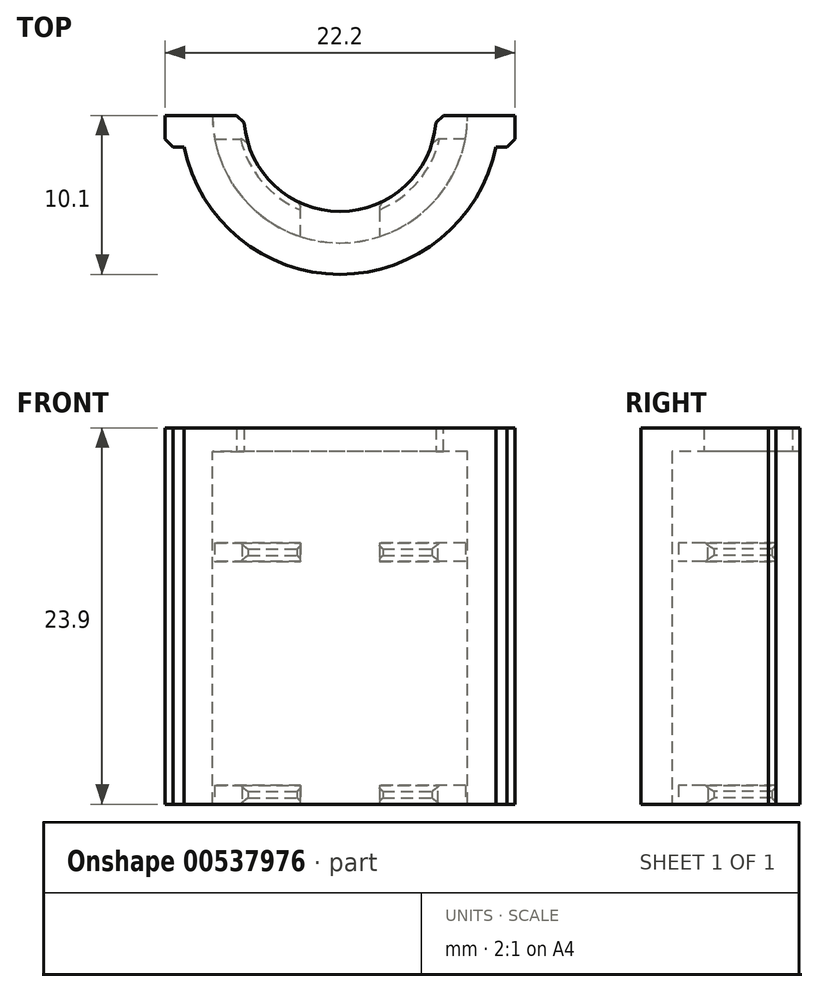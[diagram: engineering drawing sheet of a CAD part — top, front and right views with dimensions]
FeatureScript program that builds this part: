
annotation { "Feature Type Name" : "Feature", "Feature Type Description" : "" }
export const myFeature = defineFeature(function(context is Context, id is Id, definition is map)
    precondition{}
    {
        {
            var Q0;
            Q0=qCreatedBy(makeId("Front.planeOp"),FACE);
            var sketch = newSketch(context, id + "F0", { "sketchPlane" : qUnion([Q0])});
            skLineSegment(sketch, "E0.bottom", {"start": v(-8.1, 0) * mm, "end": v(-10.1, 0) * mm});
            skLineSegment(sketch, "E0.top", {"start": v(-8.1, 29) * mm, "end": v(-10.1, 29) * mm});
            skLineSegment(sketch, "E0.left", {"start": v(-8.1, 0) * mm, "end": v(-8.1, 29) * mm});
            skLineSegment(sketch, "E0.right", {"start": v(-10.1, 0) * mm, "end": v(-10.1, 29) * mm});
            skLineSegment(sketch, "E1.bottom", {"start": v(-8.1, 23.2) * mm, "end": v(-6.1, 23.2) * mm});
            skLineSegment(sketch, "E1.top", {"start": v(-8.1, 22) * mm, "end": v(-6.1, 22) * mm});
            skLineSegment(sketch, "E1.left", {"start": v(-8.1, 23.2) * mm, "end": v(-8.1, 22) * mm});
            skLineSegment(sketch, "E1.right", {"start": v(-6.1, 23.2) * mm, "end": v(-6.1, 22) * mm});
            skLineSegment(sketch, "E2", {"start": v(0, 0) * mm, "end": v(0, 37.94) * mm, "construction": true});
            skLineSegment(sketch, "E3.bottom", {"start": v(-8.1, 17) * mm, "end": v(-6.1, 17) * mm});
            skLineSegment(sketch, "E3.top", {"start": v(-8.1, 15.8) * mm, "end": v(-6.1, 15.8) * mm});
            skLineSegment(sketch, "E3.left", {"start": v(-8.1, 17) * mm, "end": v(-8.1, 15.8) * mm});
            skLineSegment(sketch, "E3.right", {"start": v(-6.1, 17) * mm, "end": v(-6.1, 15.8) * mm});
            skLineSegment(sketch, "E4.bottom", {"start": v(-8.1, 7.8) * mm, "end": v(-6.1, 7.8) * mm});
            skLineSegment(sketch, "E4.top", {"start": v(-8.1, 6.6) * mm, "end": v(-6.1, 6.6) * mm});
            skLineSegment(sketch, "E4.left", {"start": v(-8.1, 7.8) * mm, "end": v(-8.1, 6.6) * mm});
            skLineSegment(sketch, "E4.right", {"start": v(-6.1, 7.8) * mm, "end": v(-6.1, 6.6) * mm});
            skLineSegment(sketch, "E5.bottom", {"start": v(-8.1, 13.9) * mm, "end": v(-6.1, 13.9) * mm});
            skLineSegment(sketch, "E5.top", {"start": v(-8.1, 12.7) * mm, "end": v(-6.1, 12.7) * mm});
            skLineSegment(sketch, "E5.left", {"start": v(-8.1, 13.9) * mm, "end": v(-8.1, 12.7) * mm});
            skLineSegment(sketch, "E5.right", {"start": v(-6.1, 13.9) * mm, "end": v(-6.1, 12.7) * mm});
            skLineSegment(sketch, "E6.bottom", {"start": v(-10.1, 29) * mm, "end": v(-6.1, 29) * mm});
            skLineSegment(sketch, "E6.top", {"start": v(-10.1, 30.5) * mm, "end": v(-6.1, 30.5) * mm});
            skLineSegment(sketch, "E6.left", {"start": v(-10.1, 29) * mm, "end": v(-10.1, 30.5) * mm});
            skLineSegment(sketch, "E6.right", {"start": v(-6.1, 29) * mm, "end": v(-6.1, 30.5) * mm});
            skSolve(sketch);
        }
        {
            var Q0;
            {var subQ3=sQuery(id+"F0.wireOp",EDGE,"E0.bottom");Q0=makeQuery(id+"F0.imprint","IMPRINT",FACE,{"disambiguationData":[TD([[makeQuery(id+"F0.imprint","IMPRINT",EDGE,{"derivedFrom":subQ3}),-1.0]])]});}
            var Q1;
            Q1=makeQuery(id+"F0.imprint","IMPRINT",FACE,{"disambiguationData":[TD([[makeQuery(id+"F0.imprint","IMPRINT",EDGE,{"derivedFrom":sQuery(id+"F0.wireOp",EDGE,"E1.bottom")}),-1.0]])]});
            var Q2;
            Q2=makeQuery(id+"F0.imprint","IMPRINT",FACE,{"disambiguationData":[TD([[makeQuery(id+"F0.imprint","IMPRINT",EDGE,{"derivedFrom":sQuery(id+"F0.wireOp",EDGE,"E4.bottom")}),-1.0]])]});
            var Q3;
            Q3=makeQuery(id+"F0.imprint","IMPRINT",FACE,{"disambiguationData":[TD([[makeQuery(id+"F0.imprint","IMPRINT",EDGE,{"derivedFrom":sQuery(id+"F0.wireOp",EDGE,"P9eNyCsC-jT8K-Uow4-PnuW-2JQdisNrIWnP.bottom")}),-1.0]])]});
            var Q4;
            Q4=makeQuery(id+"F0.imprint","IMPRINT",FACE,{"disambiguationData":[TD([[makeQuery(id+"F0.imprint","IMPRINT",EDGE,{"derivedFrom":sQuery(id+"F0.wireOp",EDGE,"MsjulPPt-OwuK-sYkB-IQlA-wEg1vznDjQIO.bottom")}),-1.0]])]});
            var Q5;
            Q5=makeQuery(id+"F0.imprint","IMPRINT",FACE,{"disambiguationData":[TD([[makeQuery(id+"F0.imprint","IMPRINT",EDGE,{"derivedFrom":sQuery(id+"F0.wireOp",EDGE,"1A2XH9Hr-huH4-Xs39-ezpS-GpKjiSIjocRw.bottom")}),1.0]])]});
            var Q6;
            Q6=makeQuery(id+"F0.imprint","IMPRINT",FACE,{"disambiguationData":[TD([[makeQuery(id+"F0.imprint","IMPRINT",EDGE,{"derivedFrom":sQuery(id+"F0.wireOp",EDGE,"E6.top")}),-1.0]])]});
            var Q7;
            Q7=sQuery(id+"F0.wireOp",EDGE,"E2");
            revolve(context, id + "F1", {"entities" : qUnion([Q0, Q1, Q2, Q3, Q4, Q5, Q6]), "axis" : qUnion([Q7]), "revolveType" : RevolveType.ONE_DIRECTION, "angle" : 180 * degree});
        }
        {
            var Q0;
            Q0=makeQuery(id+"F1.opRevolve","SWEPT_FACE",FACE,{"disambiguationData":[OSD([sQuery(id+"F0.wireOp",EDGE,"E0.bottom")])]});
            var sketch = newSketch(context, id + "F2", { "sketchPlane" : qUnion([Q0])});
            skArc(sketch, "E7", {"start": v(2.5, 7.7) * mm, "mid": v(0, 8.1) * mm, "end": v(-2.5, 7.7) * mm});
            skLineSegment(sketch, "E8", {"start": v(2.5, 7.7) * mm, "end": v(2.5, 5.56) * mm});
            skLineSegment(sketch, "E9", {"start": v(2.5, 5.56) * mm, "end": v(-2.5, 5.56) * mm});
            skLineSegment(sketch, "E10", {"start": v(-2.5, 5.56) * mm, "end": v(-2.5, 7.7) * mm});
            skLineSegment(sketch, "E11", {"start": v(-5.91, 1.5) * mm, "end": v(-7.96, 1.5) * mm});
            skLineSegment(sketch, "E12", {"start": v(-5.91, 1.5) * mm, "end": v(-5.91, 0) * mm});
            skLineSegment(sketch, "E13", {"start": v(-5.91, 0) * mm, "end": v(-8.1, 0) * mm});
            skArc(sketch, "E14", {"start": v(-7.96, 1.5) * mm, "mid": v(-8.06, 0.75) * mm, "end": v(-8.1, 0) * mm});
            skLineSegment(sketch, "E15.MirrorCS", {"start": v(5.91, 1.5) * mm, "end": v(5.91, 0) * mm});
            skLineSegment(sketch, "E16.MirrorCS", {"start": v(5.91, 1.5) * mm, "end": v(7.96, 1.5) * mm});
            skLineSegment(sketch, "E17.MirrorCS", {"start": v(5.91, 0) * mm, "end": v(8.1, 0) * mm});
            skArc(sketch, "E18.MirrorCS", {"start": v(7.96, 1.5) * mm, "mid": v(8.06, 0.75) * mm, "end": v(8.1, 0) * mm});
            skSolve(sketch);
        }
        {
            var Q0;
            Q0=makeQuery(id+"F2.imprint","IMPRINT",FACE,{"disambiguationData":[TD([[makeQuery(id+"F2.imprint","IMPRINT",EDGE,{"derivedFrom":sQuery(id+"F2.wireOp",EDGE,"E7")}),1.0]])]});
            var Q1;
            Q1=makeQuery(id+"F2.imprint","IMPRINT",FACE,{"disambiguationData":[TD([[makeQuery(id+"F2.imprint","IMPRINT",EDGE,{"derivedFrom":sQuery(id+"F2.wireOp",EDGE,"E15.MirrorCS")}),1.0]])]});
            var Q2;
            Q2=makeQuery(id+"F2.imprint","IMPRINT",FACE,{"disambiguationData":[TD([[makeQuery(id+"F2.imprint","IMPRINT",EDGE,{"derivedFrom":sQuery(id+"F2.wireOp",EDGE,"E11")}),1.0]])]});
            var Q3;
            Q3=makeQuery(id+"F1.opRevolve","SWEPT_FACE",FACE,{"disambiguationData":[OSD([sQuery(id+"F0.wireOp",EDGE,"E6.bottom")])]});
            extrude(context, id + "F3", {"entities" : qUnion([Q0, Q1, Q2]), "operationType" : NewBodyOperationType.REMOVE, "endBound" : BoundingType.UP_TO_SURFACE, "oppositeDirection" : true, "depth" : 25 * mm, "endBoundEntityFace" : qUnion([Q3]), "offsetDistance" : 25 * mm});
        }
        {
            var Q0;
            Q0=makeQuery(id+"F1.opRevolve","SWEPT_FACE",FACE,{"disambiguationData":[OSD([sQuery(id+"F0.wireOp",EDGE,"E0.bottom")])]});
            var sketch = newSketch(context, id + "F4", { "sketchPlane" : qUnion([Q0])});
            skLineSegment(sketch, "E19.bottom", {"start": v(-9.1, 0) * mm, "end": v(-11.1, 0) * mm});
            skLineSegment(sketch, "E19.top", {"start": v(-9.1, 2) * mm, "end": v(-11.1, 2) * mm});
            skLineSegment(sketch, "E19.left", {"start": v(-9.1, 0) * mm, "end": v(-9.1, 2) * mm});
            skLineSegment(sketch, "E19.right", {"start": v(-11.1, 0) * mm, "end": v(-11.1, 2) * mm});
            skLineSegment(sketch, "E20.MirrorCS", {"start": v(9.1, 2) * mm, "end": v(11.1, 2) * mm});
            skLineSegment(sketch, "E21.MirrorCS", {"start": v(9.1, 0) * mm, "end": v(9.1, 2) * mm});
            skLineSegment(sketch, "E22.MirrorCS", {"start": v(9.1, 0) * mm, "end": v(11.1, 0) * mm});
            skLineSegment(sketch, "E23.MirrorCS", {"start": v(11.1, 0) * mm, "end": v(11.1, 2) * mm});
            skSolve(sketch);
        }
        {
            var Q0;
            {var subQ0=sQuery(id+"F4.wireOp",EDGE,"E23.MirrorCS");Q0=makeQuery(id+"F4.imprint","IMPRINT",FACE,{"disambiguationData":[TD([[makeQuery(id+"F4.imprint","IMPRINT",EDGE,{"derivedFrom":subQ0}),1.0]])]});}
            var Q1;
            {var subQ3=sQuery(id+"F4.wireOp",EDGE,"E19.right");Q1=makeQuery(id+"F4.imprint","IMPRINT",FACE,{"disambiguationData":[TD([[makeQuery(id+"F4.imprint","IMPRINT",EDGE,{"derivedFrom":subQ3}),-1.0]])]});}
            var Q2;
            Q2=makeQuery(id+"F1.opRevolve","SWEPT_FACE",FACE,{"disambiguationData":[OSD([sQuery(id+"F0.wireOp",EDGE,"E6.top")])]});
            extrude(context, id + "F5", {"entities" : qUnion([Q0, Q1]), "operationType" : NewBodyOperationType.ADD, "endBound" : BoundingType.UP_TO_SURFACE, "oppositeDirection" : true, "depth" : 25 * mm, "endBoundEntityFace" : qUnion([Q2]), "offsetDistance" : 25 * mm});
        }
        {
            var Q0;
            {var subQ7=sQuery(id+"F4.wireOp",EDGE,"E19.left");Q0=makeQuery(id+"F4.imprint","IMPRINT",FACE,{"disambiguationData":[TD([[makeQuery(id+"F4.imprint","IMPRINT",EDGE,{"derivedFrom":subQ7}),-1.0]])]});}
            var Q1;
            {var subQ3=sQuery(id+"F4.wireOp",EDGE,"E19.right");Q1=makeQuery(id+"F4.imprint","IMPRINT",FACE,{"disambiguationData":[TD([[makeQuery(id+"F4.imprint","IMPRINT",EDGE,{"derivedFrom":subQ3}),-1.0]])]});}
            var Q2;
            {var subQ4=sQuery(id+"F4.wireOp",EDGE,"E19.left");Q2=makeQuery(id+"F4.imprint","IMPRINT",FACE,{"disambiguationData":[TD([[makeQuery(id+"F4.imprint","IMPRINT",EDGE,{"derivedFrom":subQ4}),1.0]])]});}
            var Q3;
            {var subQ1=sQuery(id+"F2.wireOp",EDGE,"E7");Q3=makeQuery(id+"F2.imprint","IMPRINT",FACE,{"disambiguationData":[TD([[makeQuery(id+"F2.imprint","IMPRINT",EDGE,{"derivedFrom":subQ1}),-1.0]])]});}
            var Q4;
            {var subQ0=sQuery(id+"F4.wireOp",EDGE,"E23.MirrorCS");Q4=makeQuery(id+"F4.imprint","IMPRINT",FACE,{"disambiguationData":[TD([[makeQuery(id+"F4.imprint","IMPRINT",EDGE,{"derivedFrom":subQ0}),1.0]])]});}
            var Q5;
            {var subQ1=sQuery(id+"F0.wireOp",EDGE,"E4.top");Q5=makeQuery(id+"F3.boolean.opBoolean","SPLIT",FACE,{"disambiguationData":[TD([makeQuery(id+"F3.opExtrude","SWEPT_FACE",FACE,{"disambiguationData":[OSD([sQuery(id+"F2.wireOp",EDGE,"E10")])]})])],"derivedFrom":makeQuery(id+"F1.opRevolve","SWEPT_FACE",FACE,{"disambiguationData":[OSD([subQ1])]})});}
            extrude(context, id + "F6", {"entities" : qUnion([Q0, Q1, Q2, Q3, Q4]), "operationType" : NewBodyOperationType.REMOVE, "endBound" : BoundingType.UP_TO_SURFACE, "oppositeDirection" : true, "depth" : 25 * mm, "endBoundEntityFace" : qUnion([Q5]), "offsetDistance" : 25 * mm});
        }
        {
            var Q0;
            Q0=makeQuery(id+"F5.opExtrude","SWEPT_EDGE",EDGE,{"disambiguationData":[OSD([sQuery(id+"F4.wireOp",EDGE,"E19.top"),sQuery(id+"F4.wireOp",EDGE,"E19.right")])]});
            var Q1;
            Q1=makeQuery(id+"F5.opExtrude","SWEPT_EDGE",EDGE,{"disambiguationData":[OSD([sQuery(id+"F4.wireOp",EDGE,"E20.MirrorCS"),sQuery(id+"F4.wireOp",EDGE,"E23.MirrorCS")])]});
            var Q2;
            {var subQ0=sQuery(id+"F4.wireOp",EDGE,"E20.MirrorCS");var subQ1=sQuery(id+"F0.wireOp",EDGE,"E0.top");Q2=makeQuery(id+"F5.opExtrude","TWEAK_EDGE",EDGE,{"derivedFrom":[makeQuery(id+"FyCmuYdCQNgRQ9M_1.boolean.opBoolean","MERGE",FACE,{"derivedFrom":[makeQuery(id+"F1.opRevolve","SWEPT_FACE",FACE,{"disambiguationData":[OSD([subQ1])]}),makeQuery(id+"FyCmuYdCQNgRQ9M_1.opExtrude","CAP_FACE",FACE,{"disambiguationData":[OSD([subQ1,sQuery(id+"F0.wireOp",EDGE,"E0.left"),sQuery(id+"FUxLFSoFdhw2Clz_1.wireOp",EDGE,"mArDFc7e-Xm5c-g4cF-6cxH-YNcMVIsHVx5U")])],"isStart":true})]}),makeQuery(id+"F4.imprint","IMPRINT",EDGE,{"disambiguationData":[TD([[makeQuery(id+"F4.imprint","INTERSECT",VERTEX,{"derivedFrom":[subQ0,sQuery(id+"F4.wireOp",EDGE,"E23.MirrorCS")]}),1.0]])],"derivedFrom":subQ0})]});}
            var Q3;
            Q3=makeQuery(id+"F5.opExtrude","CAP_EDGE",EDGE,{"disambiguationData":[OSD([sQuery(id+"F4.wireOp",EDGE,"E20.MirrorCS")])],"isStart":true});
            var Q4;
            {var subQ0=sQuery(id+"F4.wireOp",EDGE,"E19.top");var subQ1=sQuery(id+"F0.wireOp",EDGE,"E0.top");Q4=makeQuery(id+"F5.opExtrude","TWEAK_EDGE",EDGE,{"derivedFrom":[makeQuery(id+"FyCmuYdCQNgRQ9M_1.boolean.opBoolean","MERGE",FACE,{"derivedFrom":[makeQuery(id+"F1.opRevolve","SWEPT_FACE",FACE,{"disambiguationData":[OSD([subQ1])]}),makeQuery(id+"FyCmuYdCQNgRQ9M_1.opExtrude","CAP_FACE",FACE,{"disambiguationData":[OSD([subQ1,sQuery(id+"F0.wireOp",EDGE,"E0.left"),sQuery(id+"FUxLFSoFdhw2Clz_1.wireOp",EDGE,"mArDFc7e-Xm5c-g4cF-6cxH-YNcMVIsHVx5U")])],"isStart":true})]}),makeQuery(id+"F4.imprint","IMPRINT",EDGE,{"disambiguationData":[TD([[makeQuery(id+"F4.imprint","INTERSECT",VERTEX,{"derivedFrom":[subQ0,sQuery(id+"F4.wireOp",EDGE,"E19.right")]}),1.0]])],"derivedFrom":subQ0})]});}
            var Q5;
            Q5=makeQuery(id+"F5.opExtrude","CAP_EDGE",EDGE,{"disambiguationData":[OSD([sQuery(id+"F4.wireOp",EDGE,"E19.top")])],"isStart":true});
            var Q6;
            Q6=makeQuery(id+"F1.opRevolve","SWEPT_EDGE",EDGE,{"disambiguationData":[OSD([sQuery(id+"F0.wireOp",EDGE,"E0.top"),sQuery(id+"F0.wireOp",EDGE,"E0.right")])]});
            var Q7;
            {var subQ0=sQuery(id+"F0.wireOp",EDGE,"E0.right");var subQ1=sQuery(id+"F0.wireOp",EDGE,"E0.bottom");var subQ2=makeQuery(id+"F1.opRevolve","SWEPT_EDGE",EDGE,{"disambiguationData":[OSD([subQ1,subQ0])]});Q7=makeQuery(id+"F6.boolean.opBoolean","TWEAK_EDGE",EDGE,{"derivedFrom":[makeQuery(id+"F6.opExtrude","CAP_EDGE",EDGE,{"disambiguationData":[OSD([subQ1,subQ0]),TDD([makeQuery(id+"F2.imprint","IMPRINT",EDGE,{"derivedFrom":subQ2})])],"isStart":false}),makeQuery(id+"F6.opExtrude","CAP_EDGE",EDGE,{"disambiguationData":[OSD([subQ1,subQ0]),TDD([makeQuery(id+"F4.imprint","IMPRINT",EDGE,{"disambiguationData":[TD([[makeQuery(id+"F4.imprint","INTERSECT",VERTEX,{"derivedFrom":[subQ2,sQuery(id+"F4.wireOp",EDGE,"E19.top")]}),1.0]])],"derivedFrom":subQ2})])],"isStart":false})]});}
            var Q8;
            {var subQ0=sQuery(id+"F0.wireOp",EDGE,"E0.bottom");var subQ1=sQuery(id+"F0.wireOp",EDGE,"E0.left");Q8=makeQuery(id+"F3.boolean.opBoolean","MERGE",EDGE,{"derivedFrom":[makeQuery(id+"F1.opRevolve","CAP_EDGE",EDGE,{"disambiguationData":[OSD([subQ1]),TDD([makeQuery(id+"F0.imprint","IMPRINT",EDGE,{"disambiguationData":[TD([[makeQuery(id+"F0.imprint","INTERSECT",VERTEX,{"derivedFrom":[subQ0,subQ1]}),-1.0]])],"derivedFrom":subQ1})])],"isStart":false}),makeQuery(id+"F1.opRevolve","CAP_EDGE",EDGE,{"disambiguationData":[OSD([subQ1,sQuery(id+"F0.wireOp",EDGE,"E3.left"),sQuery(id+"F0.wireOp",EDGE,"E5.left")])],"isStart":false}),makeQuery(id+"F1.opRevolve","CAP_EDGE",EDGE,{"disambiguationData":[OSD([subQ1]),TDD([makeQuery(id+"F0.imprint","IMPRINT",EDGE,{"disambiguationData":[TD([[makeQuery(id+"F0.imprint","INTERSECT",VERTEX,{"derivedFrom":[subQ1,sQuery(id+"F0.wireOp",EDGE,"E6.bottom")]}),1.0]])],"derivedFrom":subQ1})])],"isStart":false}),makeQuery(id+"F3.opExtrude","SWEPT_EDGE",EDGE,{"disambiguationData":[OSD([subQ0,sQuery(id+"F2.wireOp",EDGE,"E17.MirrorCS"),sQuery(id+"F2.wireOp",EDGE,"E18.MirrorCS")])]})]});}
            var Q9;
            {var subQ0=sQuery(id+"F0.wireOp",EDGE,"E0.bottom");var subQ1=sQuery(id+"F0.wireOp",EDGE,"E0.left");Q9=makeQuery(id+"F3.boolean.opBoolean","MERGE",EDGE,{"derivedFrom":[makeQuery(id+"F1.opRevolve","CAP_EDGE",EDGE,{"disambiguationData":[OSD([subQ1]),TDD([makeQuery(id+"F0.imprint","IMPRINT",EDGE,{"disambiguationData":[TD([[makeQuery(id+"F0.imprint","INTERSECT",VERTEX,{"derivedFrom":[subQ0,subQ1]}),-1.0]])],"derivedFrom":subQ1})])],"isStart":true}),makeQuery(id+"F1.opRevolve","CAP_EDGE",EDGE,{"disambiguationData":[OSD([subQ1,sQuery(id+"F0.wireOp",EDGE,"E3.left"),sQuery(id+"F0.wireOp",EDGE,"E5.left")])],"isStart":true}),makeQuery(id+"F1.opRevolve","CAP_EDGE",EDGE,{"disambiguationData":[OSD([subQ1]),TDD([makeQuery(id+"F0.imprint","IMPRINT",EDGE,{"disambiguationData":[TD([[makeQuery(id+"F0.imprint","INTERSECT",VERTEX,{"derivedFrom":[subQ1,sQuery(id+"F0.wireOp",EDGE,"E6.bottom")]}),1.0]])],"derivedFrom":subQ1})])],"isStart":true}),makeQuery(id+"F3.opExtrude","SWEPT_EDGE",EDGE,{"disambiguationData":[OSD([subQ0,sQuery(id+"F2.wireOp",EDGE,"E13"),sQuery(id+"F2.wireOp",EDGE,"E14")])]})]});}
            var Q10;
            Q10=makeQuery(id+"F6.boolean.opBoolean","COPY",EDGE,{"derivedFrom":makeQuery(id+"F6.opExtrude","CAP_EDGE",EDGE,{"disambiguationData":[OSD([sQuery(id+"F0.wireOp",EDGE,"E0.bottom"),sQuery(id+"F4.wireOp",EDGE,"E19.bottom")])],"isStart":false})});
            var Q11;
            {var subQ0=sQuery(id+"F0.wireOp",EDGE,"E0.bottom");var subQ1=makeQuery(id+"F1.opRevolve","CAP_EDGE",EDGE,{"disambiguationData":[OSD([subQ0])],"isStart":false});var subQ2=sQuery(id+"F4.wireOp",EDGE,"E22.MirrorCS");Q11=makeQuery(id+"F6.boolean.opBoolean","TWEAK_EDGE",EDGE,{"derivedFrom":[makeQuery(id+"F6.opExtrude","CAP_EDGE",EDGE,{"disambiguationData":[OSD([subQ0]),TDD([makeQuery(id+"F2.imprint","IMPRINT",EDGE,{"derivedFrom":subQ1})])],"isStart":false}),makeQuery(id+"F6.opExtrude","CAP_EDGE",EDGE,{"disambiguationData":[OSD([subQ2])],"isStart":false}),makeQuery(id+"F6.opExtrude","CAP_EDGE",EDGE,{"disambiguationData":[OSD([subQ0]),TDD([makeQuery(id+"F4.imprint","IMPRINT",EDGE,{"disambiguationData":[TD([[makeQuery(id+"F4.imprint","INTERSECT",VERTEX,{"derivedFrom":[subQ1,makeQuery(id+"F1.opRevolve","SWEPT_EDGE",EDGE,{"disambiguationData":[OSD([subQ0,sQuery(id+"F0.wireOp",EDGE,"E0.left")])]})]}),-1.0]])],"derivedFrom":subQ1})])],"isStart":false})]});}
            var Q12;
            Q12=makeQuery(id+"F1.opRevolve","CAP_EDGE",EDGE,{"disambiguationData":[OSD([sQuery(id+"F0.wireOp",EDGE,"E6.right")])],"isStart":true});
            var Q13;
            Q13=makeQuery(id+"F1.opRevolve","CAP_EDGE",EDGE,{"disambiguationData":[OSD([sQuery(id+"F0.wireOp",EDGE,"E6.right")])],"isStart":false});
            chamfer(context, id + "F7", {"entities" : qUnion([Q0, Q1, Q2, Q3, Q4, Q5, Q6, Q7, Q8, Q9, Q10, Q11, Q12, Q13]), "width" : .5 * mm});
        }
        {
            var Q0;
            Q0=makeQuery(id+"F3.boolean.opBoolean","SPLIT",FACE,{"disambiguationData":[TD([makeQuery(id+"F3.opExtrude","SWEPT_FACE",FACE,{"disambiguationData":[OSD([sQuery(id+"F2.wireOp",EDGE,"E8")])]})])],"derivedFrom":makeQuery(id+"F1.opRevolve","SWEPT_FACE",FACE,{"disambiguationData":[OSD([sQuery(id+"F0.wireOp",EDGE,"E4.right")])]})});
            var Q1;
            Q1=makeQuery(id+"F3.boolean.opBoolean","SPLIT",FACE,{"disambiguationData":[TD([makeQuery(id+"F3.opExtrude","SWEPT_FACE",FACE,{"disambiguationData":[OSD([sQuery(id+"F2.wireOp",EDGE,"E10")])]})])],"derivedFrom":makeQuery(id+"F1.opRevolve","SWEPT_FACE",FACE,{"disambiguationData":[OSD([sQuery(id+"F0.wireOp",EDGE,"E4.right")])]})});
            var Q2;
            Q2=makeQuery(id+"F3.boolean.opBoolean","SPLIT",FACE,{"disambiguationData":[TD([makeQuery(id+"F3.opExtrude","SWEPT_FACE",FACE,{"disambiguationData":[OSD([sQuery(id+"F2.wireOp",EDGE,"E10")])]})])],"derivedFrom":makeQuery(id+"F1.opRevolve","SWEPT_FACE",FACE,{"disambiguationData":[OSD([sQuery(id+"F0.wireOp",EDGE,"E1.right")])]})});
            var Q3;
            Q3=makeQuery(id+"F3.boolean.opBoolean","SPLIT",FACE,{"disambiguationData":[TD([makeQuery(id+"F3.opExtrude","SWEPT_FACE",FACE,{"disambiguationData":[OSD([sQuery(id+"F2.wireOp",EDGE,"E8")])]})])],"derivedFrom":makeQuery(id+"F1.opRevolve","SWEPT_FACE",FACE,{"disambiguationData":[OSD([sQuery(id+"F0.wireOp",EDGE,"E1.right")])]})});
            chamfer(context, id + "F8", {"entities" : qUnion([Q0, Q1, Q2, Q3]), "width" : .4 * mm});
        }
    });
